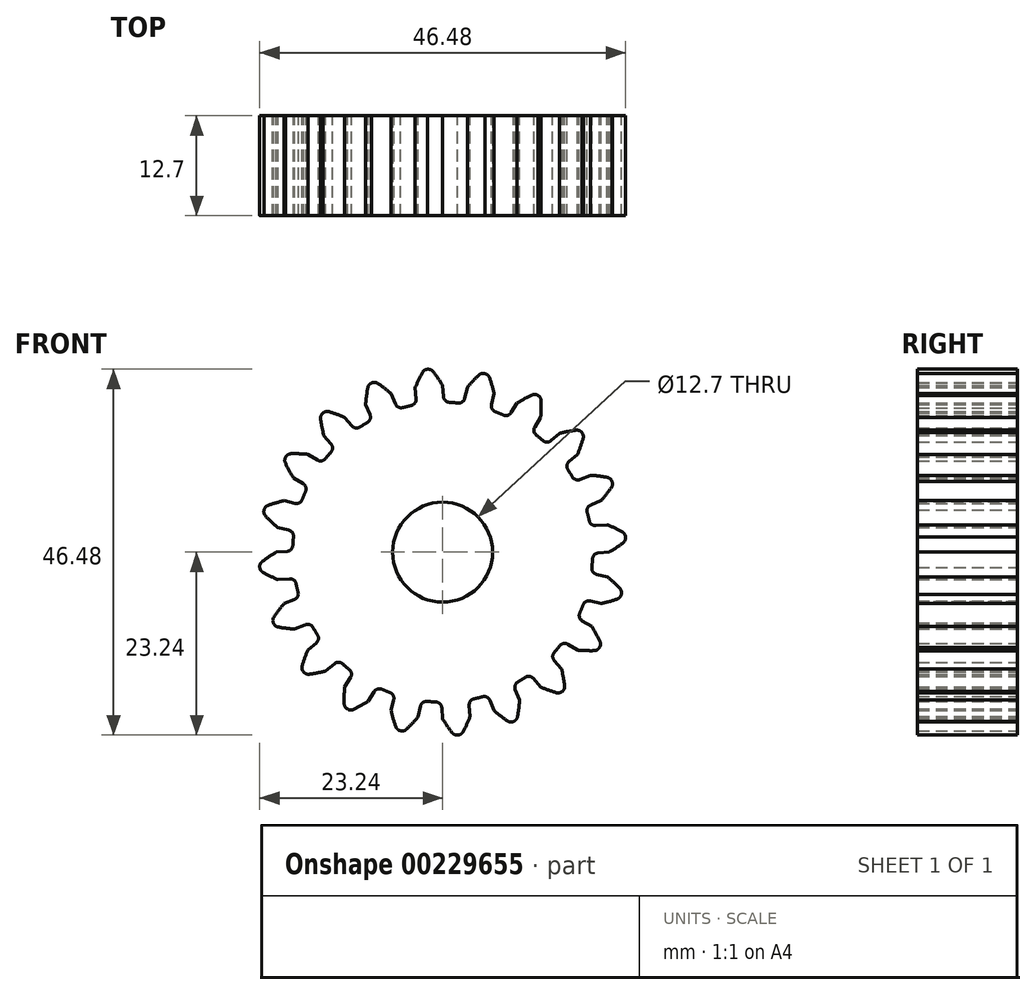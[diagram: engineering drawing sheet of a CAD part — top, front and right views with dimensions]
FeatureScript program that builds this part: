
annotation { "Feature Type Name" : "Feature", "Feature Type Description" : "" }
export const myFeature = defineFeature(function(context is Context, id is Id, definition is map)
    precondition{}
    {
        {
            var Q0;
            Q0=qCreatedBy(makeId("Front.planeOp"),FACE);
            var sketch = newSketch(context, id + "F0", { "sketchPlane" : qUnion([Q0])});
            skArc(sketch, "E0", {"start": v(-4, 18.63) * mm, "mid": v(-12.3, -14.54) * mm, "end": v(19.03, -0.86) * mm});
            skArc(sketch, "E1.trimOffspring", {"start": v(0, 21.17) * mm, "mid": v(-0.57, 22.06) * mm, "end": v(-1.2, 22.93) * mm});
            skLineSegment(sketch, "E2", {"start": v(-1.82, 23.24) * mm, "end": v(-1.92, 23.24) * mm});
            skLineSegment(sketch, "E3", {"start": v(0, 21.17) * mm, "end": v(0.11, 19.76) * mm});
            skLineSegment(sketch, "E4.MirrorCS", {"start": v(-2.01, 23.22) * mm, "end": v(-1.92, 23.24) * mm});
            skArc(sketch, "E5.MirrorCS", {"start": v(-3.49, 20.9) * mm, "mid": v(-3.06, 21.87) * mm, "end": v(-2.58, 22.82) * mm});
            skLineSegment(sketch, "E6.MirrorCS", {"start": v(-3.49, 20.9) * mm, "end": v(-3.38, 19.46) * mm});
            skPoint(sketch, "E7.visualSharp", {"position": v(0.17, 19.05) * mm});
            skArc(sketch, "E7.filletArc", {"start": v(0.11, 19.76) * mm, "mid": v(0.35, 19.25) * mm, "end": v(0.86, 19.03) * mm});
            skPoint(sketch, "E8.visualSharp", {"position": v(-3.32, 18.76) * mm});
            skArc(sketch, "E8.filletArc", {"start": v(-4, 18.63) * mm, "mid": v(-3.53, 18.93) * mm, "end": v(-3.38, 19.46) * mm});
            skPoint(sketch, "E9.visualSharp", {"position": v(-2.39, 23.16) * mm});
            skArc(sketch, "E9.filletArc", {"start": v(-2.01, 23.22) * mm, "mid": v(-2.34, 23.09) * mm, "end": v(-2.58, 22.82) * mm});
            skPoint(sketch, "E10.visualSharp", {"position": v(-1.44, 23.24) * mm});
            skArc(sketch, "E10.filletArc", {"start": v(-1.2, 22.93) * mm, "mid": v(-1.47, 23.16) * mm, "end": v(-1.82, 23.24) * mm});
            skArc(sketch, "E11.1.0", {"start": v(-9.56, 16.48) * mm, "mid": v(-9.2, 16.9) * mm, "end": v(-9.22, 17.46) * mm});
            skLineSegment(sketch, "E11.1.1", {"start": v(-9.77, 18.8) * mm, "end": v(-9.22, 17.46) * mm});
            skArc(sketch, "E11.1.2", {"start": v(-9.77, 18.8) * mm, "mid": v(-9.67, 19.85) * mm, "end": v(-9.5, 20.9) * mm});
            skArc(sketch, "E11.1.3", {"start": v(-9.09, 21.47) * mm, "mid": v(-9.36, 21.24) * mm, "end": v(-9.5, 20.9) * mm});
            skLineSegment(sketch, "E11.1.4", {"start": v(-9.09, 21.47) * mm, "end": v(-9, 21.5) * mm});
            skLineSegment(sketch, "E11.1.5", {"start": v(-8.92, 21.54) * mm, "end": v(-9, 21.5) * mm});
            skArc(sketch, "E11.1.6", {"start": v(-8.23, 21.44) * mm, "mid": v(-8.56, 21.57) * mm, "end": v(-8.92, 21.54) * mm});
            skArc(sketch, "E11.1.7", {"start": v(-6.54, 20.13) * mm, "mid": v(-7.36, 20.8) * mm, "end": v(-8.23, 21.44) * mm});
            skLineSegment(sketch, "E11.1.8", {"start": v(-6.54, 20.13) * mm, "end": v(-6, 18.82) * mm});
            skArc(sketch, "E11.1.9", {"start": v(-6, 18.82) * mm, "mid": v(-5.62, 18.42) * mm, "end": v(-5.06, 18.37) * mm});
            skArc(sketch, "E11.2.0", {"start": v(-14.18, 12.72) * mm, "mid": v(-13.98, 13.24) * mm, "end": v(-14.17, 13.76) * mm});
            skLineSegment(sketch, "E11.2.1", {"start": v(-15.1, 14.85) * mm, "end": v(-14.17, 13.76) * mm});
            skArc(sketch, "E11.2.2", {"start": v(-15.1, 14.85) * mm, "mid": v(-15.33, 15.9) * mm, "end": v(-15.5, 16.95) * mm});
            skArc(sketch, "E11.2.3", {"start": v(-15.28, 17.6) * mm, "mid": v(-15.47, 17.3) * mm, "end": v(-15.5, 16.95) * mm});
            skLineSegment(sketch, "E11.2.4", {"start": v(-15.28, 17.6) * mm, "end": v(-15.21, 17.67) * mm});
            skLineSegment(sketch, "E11.2.5", {"start": v(-15.13, 17.73) * mm, "end": v(-15.21, 17.67) * mm});
            skArc(sketch, "E11.2.6", {"start": v(-14.45, 17.85) * mm, "mid": v(-14.8, 17.87) * mm, "end": v(-15.13, 17.73) * mm});
            skArc(sketch, "E11.2.7", {"start": v(-12.44, 17.12) * mm, "mid": v(-13.43, 17.51) * mm, "end": v(-14.45, 17.85) * mm});
            skLineSegment(sketch, "E11.2.8", {"start": v(-12.44, 17.12) * mm, "end": v(-11.52, 16.05) * mm});
            skArc(sketch, "E11.2.9", {"start": v(-11.52, 16.05) * mm, "mid": v(-11.03, 15.78) * mm, "end": v(-10.49, 15.9) * mm});
            skArc(sketch, "E11.3.0", {"start": v(-17.42, 7.72) * mm, "mid": v(-17.39, 8.27) * mm, "end": v(-17.73, 8.7) * mm});
            skLineSegment(sketch, "E11.3.1", {"start": v(-18.95, 9.46) * mm, "end": v(-17.73, 8.7) * mm});
            skArc(sketch, "E11.3.2", {"start": v(-18.95, 9.46) * mm, "mid": v(-19.5, 10.38) * mm, "end": v(-19.98, 11.33) * mm});
            skArc(sketch, "E11.3.3", {"start": v(-19.97, 12.02) * mm, "mid": v(-20.06, 11.68) * mm, "end": v(-19.98, 11.33) * mm});
            skLineSegment(sketch, "E11.3.4", {"start": v(-19.97, 12.02) * mm, "end": v(-19.93, 12.1) * mm});
            skLineSegment(sketch, "E11.3.5", {"start": v(-19.87, 12.18) * mm, "end": v(-19.93, 12.1) * mm});
            skArc(sketch, "E11.3.6", {"start": v(-19.25, 12.5) * mm, "mid": v(-19.6, 12.42) * mm, "end": v(-19.87, 12.18) * mm});
            skArc(sketch, "E11.3.7", {"start": v(-17.12, 12.44) * mm, "mid": v(-18.19, 12.5) * mm, "end": v(-19.25, 12.5) * mm});
            skLineSegment(sketch, "E11.3.8", {"start": v(-17.12, 12.44) * mm, "end": v(-15.92, 11.7) * mm});
            skArc(sketch, "E11.3.9", {"start": v(-15.92, 11.7) * mm, "mid": v(-15.37, 11.6) * mm, "end": v(-14.9, 11.88) * mm});
            skArc(sketch, "E11.4.0", {"start": v(-18.95, 1.96) * mm, "mid": v(-19.09, 2.5) * mm, "end": v(-19.55, 2.8) * mm});
            skLineSegment(sketch, "E11.4.1", {"start": v(-20.95, 3.14) * mm, "end": v(-19.55, 2.8) * mm});
            skArc(sketch, "E11.4.2", {"start": v(-20.95, 3.14) * mm, "mid": v(-21.74, 3.85) * mm, "end": v(-22.5, 4.6) * mm});
            skArc(sketch, "E11.4.3", {"start": v(-22.7, 5.26) * mm, "mid": v(-22.68, 4.9) * mm, "end": v(-22.5, 4.6) * mm});
            skLineSegment(sketch, "E11.4.4", {"start": v(-22.7, 5.26) * mm, "end": v(-22.7, 5.36) * mm});
            skLineSegment(sketch, "E11.4.5", {"start": v(-22.66, 5.45) * mm, "end": v(-22.7, 5.36) * mm});
            skArc(sketch, "E11.4.6", {"start": v(-22.18, 5.95) * mm, "mid": v(-22.48, 5.75) * mm, "end": v(-22.66, 5.45) * mm});
            skArc(sketch, "E11.4.7", {"start": v(-20.13, 6.54) * mm, "mid": v(-21.16, 6.27) * mm, "end": v(-22.18, 5.95) * mm});
            skLineSegment(sketch, "E11.4.8", {"start": v(-20.13, 6.54) * mm, "end": v(-18.75, 6.21) * mm});
            skArc(sketch, "E11.4.9", {"start": v(-18.75, 6.21) * mm, "mid": v(-18.2, 6.28) * mm, "end": v(-17.83, 6.7) * mm});
            skArc(sketch, "E11.5.0", {"start": v(-18.63, -4) * mm, "mid": v(-18.93, -3.53) * mm, "end": v(-19.46, -3.38) * mm});
            skLineSegment(sketch, "E11.5.1", {"start": v(-20.9, -3.49) * mm, "end": v(-19.46, -3.38) * mm});
            skArc(sketch, "E11.5.2", {"start": v(-20.9, -3.49) * mm, "mid": v(-21.87, -3.06) * mm, "end": v(-22.82, -2.58) * mm});
            skArc(sketch, "E11.5.3", {"start": v(-23.22, -2.01) * mm, "mid": v(-23.09, -2.34) * mm, "end": v(-22.82, -2.58) * mm});
            skLineSegment(sketch, "E11.5.4", {"start": v(-23.22, -2.01) * mm, "end": v(-23.24, -1.92) * mm});
            skLineSegment(sketch, "E11.5.5", {"start": v(-23.24, -1.82) * mm, "end": v(-23.24, -1.92) * mm});
            skArc(sketch, "E11.5.6", {"start": v(-22.93, -1.2) * mm, "mid": v(-23.16, -1.47) * mm, "end": v(-23.24, -1.82) * mm});
            skArc(sketch, "E11.5.7", {"start": v(-21.17, 0) * mm, "mid": v(-22.06, -0.57) * mm, "end": v(-22.93, -1.2) * mm});
            skLineSegment(sketch, "E11.5.8", {"start": v(-21.17, 0) * mm, "end": v(-19.76, 0.11) * mm});
            skArc(sketch, "E11.5.9", {"start": v(-19.76, 0.11) * mm, "mid": v(-19.25, 0.35) * mm, "end": v(-19.03, 0.86) * mm});
            skArc(sketch, "E11.6.0", {"start": v(-16.48, -9.56) * mm, "mid": v(-16.9, -9.2) * mm, "end": v(-17.46, -9.22) * mm});
            skLineSegment(sketch, "E11.6.1", {"start": v(-18.8, -9.77) * mm, "end": v(-17.46, -9.22) * mm});
            skArc(sketch, "E11.6.2", {"start": v(-18.8, -9.77) * mm, "mid": v(-19.85, -9.67) * mm, "end": v(-20.9, -9.5) * mm});
            skArc(sketch, "E11.6.3", {"start": v(-21.47, -9.09) * mm, "mid": v(-21.24, -9.36) * mm, "end": v(-20.9, -9.5) * mm});
            skLineSegment(sketch, "E11.6.4", {"start": v(-21.47, -9.09) * mm, "end": v(-21.5, -9) * mm});
            skLineSegment(sketch, "E11.6.5", {"start": v(-21.54, -8.92) * mm, "end": v(-21.5, -9) * mm});
            skArc(sketch, "E11.6.6", {"start": v(-21.44, -8.23) * mm, "mid": v(-21.57, -8.56) * mm, "end": v(-21.54, -8.92) * mm});
            skArc(sketch, "E11.6.7", {"start": v(-20.13, -6.54) * mm, "mid": v(-20.8, -7.36) * mm, "end": v(-21.44, -8.23) * mm});
            skLineSegment(sketch, "E11.6.8", {"start": v(-20.13, -6.54) * mm, "end": v(-18.82, -6) * mm});
            skArc(sketch, "E11.6.9", {"start": v(-18.82, -6) * mm, "mid": v(-18.42, -5.62) * mm, "end": v(-18.37, -5.06) * mm});
            skArc(sketch, "E11.7.0", {"start": v(-12.72, -14.18) * mm, "mid": v(-13.24, -13.98) * mm, "end": v(-13.76, -14.17) * mm});
            skLineSegment(sketch, "E11.7.1", {"start": v(-14.85, -15.1) * mm, "end": v(-13.76, -14.17) * mm});
            skArc(sketch, "E11.7.2", {"start": v(-14.85, -15.1) * mm, "mid": v(-15.9, -15.33) * mm, "end": v(-16.95, -15.5) * mm});
            skArc(sketch, "E11.7.3", {"start": v(-17.6, -15.28) * mm, "mid": v(-17.3, -15.47) * mm, "end": v(-16.95, -15.5) * mm});
            skLineSegment(sketch, "E11.7.4", {"start": v(-17.6, -15.28) * mm, "end": v(-17.67, -15.21) * mm});
            skLineSegment(sketch, "E11.7.5", {"start": v(-17.73, -15.13) * mm, "end": v(-17.67, -15.21) * mm});
            skArc(sketch, "E11.7.6", {"start": v(-17.85, -14.45) * mm, "mid": v(-17.87, -14.8) * mm, "end": v(-17.73, -15.13) * mm});
            skArc(sketch, "E11.7.7", {"start": v(-17.12, -12.44) * mm, "mid": v(-17.51, -13.43) * mm, "end": v(-17.85, -14.45) * mm});
            skLineSegment(sketch, "E11.7.8", {"start": v(-17.12, -12.44) * mm, "end": v(-16.05, -11.52) * mm});
            skArc(sketch, "E11.7.9", {"start": v(-16.05, -11.52) * mm, "mid": v(-15.78, -11.03) * mm, "end": v(-15.9, -10.49) * mm});
            skArc(sketch, "E11.8.0", {"start": v(-7.72, -17.42) * mm, "mid": v(-8.27, -17.39) * mm, "end": v(-8.7, -17.73) * mm});
            skLineSegment(sketch, "E11.8.1", {"start": v(-9.46, -18.95) * mm, "end": v(-8.7, -17.73) * mm});
            skArc(sketch, "E11.8.2", {"start": v(-9.46, -18.95) * mm, "mid": v(-10.38, -19.5) * mm, "end": v(-11.33, -19.98) * mm});
            skArc(sketch, "E11.8.3", {"start": v(-12.02, -19.97) * mm, "mid": v(-11.68, -20.06) * mm, "end": v(-11.33, -19.98) * mm});
            skLineSegment(sketch, "E11.8.4", {"start": v(-12.02, -19.97) * mm, "end": v(-12.1, -19.93) * mm});
            skLineSegment(sketch, "E11.8.5", {"start": v(-12.18, -19.87) * mm, "end": v(-12.1, -19.93) * mm});
            skArc(sketch, "E11.8.6", {"start": v(-12.5, -19.25) * mm, "mid": v(-12.42, -19.6) * mm, "end": v(-12.18, -19.87) * mm});
            skArc(sketch, "E11.8.7", {"start": v(-12.44, -17.12) * mm, "mid": v(-12.5, -18.19) * mm, "end": v(-12.5, -19.25) * mm});
            skLineSegment(sketch, "E11.8.8", {"start": v(-12.44, -17.12) * mm, "end": v(-11.7, -15.92) * mm});
            skArc(sketch, "E11.8.9", {"start": v(-11.7, -15.92) * mm, "mid": v(-11.6, -15.37) * mm, "end": v(-11.88, -14.9) * mm});
            skArc(sketch, "E11.9.0", {"start": v(-1.96, -18.95) * mm, "mid": v(-2.5, -19.09) * mm, "end": v(-2.8, -19.55) * mm});
            skLineSegment(sketch, "E11.9.1", {"start": v(-3.14, -20.95) * mm, "end": v(-2.8, -19.55) * mm});
            skArc(sketch, "E11.9.2", {"start": v(-3.14, -20.95) * mm, "mid": v(-3.85, -21.74) * mm, "end": v(-4.6, -22.5) * mm});
            skArc(sketch, "E11.9.3", {"start": v(-5.26, -22.7) * mm, "mid": v(-4.9, -22.68) * mm, "end": v(-4.6, -22.5) * mm});
            skLineSegment(sketch, "E11.9.4", {"start": v(-5.26, -22.7) * mm, "end": v(-5.36, -22.7) * mm});
            skLineSegment(sketch, "E11.9.5", {"start": v(-5.45, -22.66) * mm, "end": v(-5.36, -22.7) * mm});
            skArc(sketch, "E11.9.6", {"start": v(-5.95, -22.18) * mm, "mid": v(-5.75, -22.48) * mm, "end": v(-5.45, -22.66) * mm});
            skArc(sketch, "E11.9.7", {"start": v(-6.54, -20.13) * mm, "mid": v(-6.27, -21.16) * mm, "end": v(-5.95, -22.18) * mm});
            skLineSegment(sketch, "E11.9.8", {"start": v(-6.54, -20.13) * mm, "end": v(-6.21, -18.75) * mm});
            skArc(sketch, "E11.9.9", {"start": v(-6.21, -18.75) * mm, "mid": v(-6.28, -18.2) * mm, "end": v(-6.7, -17.83) * mm});
            skArc(sketch, "E11.10.0", {"start": v(4, -18.63) * mm, "mid": v(3.53, -18.93) * mm, "end": v(3.38, -19.46) * mm});
            skLineSegment(sketch, "E11.10.1", {"start": v(3.49, -20.9) * mm, "end": v(3.38, -19.46) * mm});
            skArc(sketch, "E11.10.2", {"start": v(3.49, -20.9) * mm, "mid": v(3.06, -21.87) * mm, "end": v(2.58, -22.82) * mm});
            skArc(sketch, "E11.10.3", {"start": v(2.01, -23.22) * mm, "mid": v(2.34, -23.09) * mm, "end": v(2.58, -22.82) * mm});
            skLineSegment(sketch, "E11.10.4", {"start": v(2.01, -23.22) * mm, "end": v(1.92, -23.24) * mm});
            skLineSegment(sketch, "E11.10.5", {"start": v(1.82, -23.24) * mm, "end": v(1.92, -23.24) * mm});
            skArc(sketch, "E11.10.6", {"start": v(1.2, -22.93) * mm, "mid": v(1.47, -23.16) * mm, "end": v(1.82, -23.24) * mm});
            skArc(sketch, "E11.10.7", {"start": v(0, -21.17) * mm, "mid": v(0.57, -22.06) * mm, "end": v(1.2, -22.93) * mm});
            skLineSegment(sketch, "E11.10.8", {"start": v(0, -21.17) * mm, "end": v(-0.11, -19.76) * mm});
            skArc(sketch, "E11.10.9", {"start": v(-0.11, -19.76) * mm, "mid": v(-0.35, -19.25) * mm, "end": v(-0.86, -19.03) * mm});
            skArc(sketch, "E11.11.0", {"start": v(9.56, -16.48) * mm, "mid": v(9.2, -16.9) * mm, "end": v(9.22, -17.46) * mm});
            skLineSegment(sketch, "E11.11.1", {"start": v(9.77, -18.8) * mm, "end": v(9.22, -17.46) * mm});
            skArc(sketch, "E11.11.2", {"start": v(9.77, -18.8) * mm, "mid": v(9.67, -19.85) * mm, "end": v(9.5, -20.9) * mm});
            skArc(sketch, "E11.11.3", {"start": v(9.09, -21.47) * mm, "mid": v(9.36, -21.24) * mm, "end": v(9.5, -20.9) * mm});
            skLineSegment(sketch, "E11.11.4", {"start": v(9.09, -21.47) * mm, "end": v(9, -21.5) * mm});
            skLineSegment(sketch, "E11.11.5", {"start": v(8.92, -21.54) * mm, "end": v(9, -21.5) * mm});
            skArc(sketch, "E11.11.6", {"start": v(8.23, -21.44) * mm, "mid": v(8.56, -21.57) * mm, "end": v(8.92, -21.54) * mm});
            skArc(sketch, "E11.11.7", {"start": v(6.54, -20.13) * mm, "mid": v(7.36, -20.8) * mm, "end": v(8.23, -21.44) * mm});
            skLineSegment(sketch, "E11.11.8", {"start": v(6.54, -20.13) * mm, "end": v(6, -18.82) * mm});
            skArc(sketch, "E11.11.9", {"start": v(6, -18.82) * mm, "mid": v(5.62, -18.42) * mm, "end": v(5.06, -18.37) * mm});
            skArc(sketch, "E11.12.0", {"start": v(14.18, -12.72) * mm, "mid": v(13.98, -13.24) * mm, "end": v(14.17, -13.76) * mm});
            skLineSegment(sketch, "E11.12.1", {"start": v(15.1, -14.85) * mm, "end": v(14.17, -13.76) * mm});
            skArc(sketch, "E11.12.2", {"start": v(15.1, -14.85) * mm, "mid": v(15.33, -15.9) * mm, "end": v(15.5, -16.95) * mm});
            skArc(sketch, "E11.12.3", {"start": v(15.28, -17.6) * mm, "mid": v(15.47, -17.3) * mm, "end": v(15.5, -16.95) * mm});
            skLineSegment(sketch, "E11.12.4", {"start": v(15.28, -17.6) * mm, "end": v(15.21, -17.67) * mm});
            skLineSegment(sketch, "E11.12.5", {"start": v(15.13, -17.73) * mm, "end": v(15.21, -17.67) * mm});
            skArc(sketch, "E11.12.6", {"start": v(14.45, -17.85) * mm, "mid": v(14.8, -17.87) * mm, "end": v(15.13, -17.73) * mm});
            skArc(sketch, "E11.12.7", {"start": v(12.44, -17.12) * mm, "mid": v(13.43, -17.51) * mm, "end": v(14.45, -17.85) * mm});
            skLineSegment(sketch, "E11.12.8", {"start": v(12.44, -17.12) * mm, "end": v(11.52, -16.05) * mm});
            skArc(sketch, "E11.12.9", {"start": v(11.52, -16.05) * mm, "mid": v(11.03, -15.78) * mm, "end": v(10.49, -15.9) * mm});
            skArc(sketch, "E11.13.0", {"start": v(17.42, -7.72) * mm, "mid": v(17.39, -8.27) * mm, "end": v(17.73, -8.7) * mm});
            skLineSegment(sketch, "E11.13.1", {"start": v(18.95, -9.46) * mm, "end": v(17.73, -8.7) * mm});
            skArc(sketch, "E11.13.2", {"start": v(18.95, -9.46) * mm, "mid": v(19.5, -10.38) * mm, "end": v(19.98, -11.33) * mm});
            skArc(sketch, "E11.13.3", {"start": v(19.97, -12.02) * mm, "mid": v(20.06, -11.68) * mm, "end": v(19.98, -11.33) * mm});
            skLineSegment(sketch, "E11.13.4", {"start": v(19.97, -12.02) * mm, "end": v(19.93, -12.1) * mm});
            skLineSegment(sketch, "E11.13.5", {"start": v(19.87, -12.18) * mm, "end": v(19.93, -12.1) * mm});
            skArc(sketch, "E11.13.6", {"start": v(19.25, -12.5) * mm, "mid": v(19.6, -12.42) * mm, "end": v(19.87, -12.18) * mm});
            skArc(sketch, "E11.13.7", {"start": v(17.12, -12.44) * mm, "mid": v(18.19, -12.5) * mm, "end": v(19.25, -12.5) * mm});
            skLineSegment(sketch, "E11.13.8", {"start": v(17.12, -12.44) * mm, "end": v(15.92, -11.7) * mm});
            skArc(sketch, "E11.13.9", {"start": v(15.92, -11.7) * mm, "mid": v(15.37, -11.6) * mm, "end": v(14.9, -11.88) * mm});
            skArc(sketch, "E11.14.0", {"start": v(18.95, -1.96) * mm, "mid": v(19.09, -2.5) * mm, "end": v(19.55, -2.8) * mm});
            skLineSegment(sketch, "E11.14.1", {"start": v(20.95, -3.14) * mm, "end": v(19.55, -2.8) * mm});
            skArc(sketch, "E11.14.2", {"start": v(20.95, -3.14) * mm, "mid": v(21.74, -3.85) * mm, "end": v(22.5, -4.6) * mm});
            skArc(sketch, "E11.14.3", {"start": v(22.7, -5.26) * mm, "mid": v(22.68, -4.9) * mm, "end": v(22.5, -4.6) * mm});
            skLineSegment(sketch, "E11.14.4", {"start": v(22.7, -5.26) * mm, "end": v(22.7, -5.36) * mm});
            skLineSegment(sketch, "E11.14.5", {"start": v(22.66, -5.45) * mm, "end": v(22.7, -5.36) * mm});
            skArc(sketch, "E11.14.6", {"start": v(22.18, -5.95) * mm, "mid": v(22.48, -5.75) * mm, "end": v(22.66, -5.45) * mm});
            skArc(sketch, "E11.14.7", {"start": v(20.13, -6.54) * mm, "mid": v(21.16, -6.27) * mm, "end": v(22.18, -5.95) * mm});
            skLineSegment(sketch, "E11.14.8", {"start": v(20.13, -6.54) * mm, "end": v(18.75, -6.21) * mm});
            skArc(sketch, "E11.14.9", {"start": v(18.75, -6.21) * mm, "mid": v(18.2, -6.28) * mm, "end": v(17.83, -6.7) * mm});
            skArc(sketch, "E11.15.0", {"start": v(18.63, 4) * mm, "mid": v(18.93, 3.53) * mm, "end": v(19.46, 3.38) * mm});
            skLineSegment(sketch, "E11.15.1", {"start": v(20.9, 3.49) * mm, "end": v(19.46, 3.38) * mm});
            skArc(sketch, "E11.15.2", {"start": v(20.9, 3.49) * mm, "mid": v(21.87, 3.06) * mm, "end": v(22.82, 2.58) * mm});
            skArc(sketch, "E11.15.3", {"start": v(23.22, 2.01) * mm, "mid": v(23.09, 2.34) * mm, "end": v(22.82, 2.58) * mm});
            skLineSegment(sketch, "E11.15.4", {"start": v(23.22, 2.01) * mm, "end": v(23.24, 1.92) * mm});
            skLineSegment(sketch, "E11.15.5", {"start": v(23.24, 1.82) * mm, "end": v(23.24, 1.92) * mm});
            skArc(sketch, "E11.15.6", {"start": v(22.93, 1.2) * mm, "mid": v(23.16, 1.47) * mm, "end": v(23.24, 1.82) * mm});
            skArc(sketch, "E11.15.7", {"start": v(21.17, 0) * mm, "mid": v(22.06, 0.57) * mm, "end": v(22.93, 1.2) * mm});
            skLineSegment(sketch, "E11.15.8", {"start": v(21.17, 0) * mm, "end": v(19.76, -0.11) * mm});
            skArc(sketch, "E11.15.9", {"start": v(19.76, -0.11) * mm, "mid": v(19.25, -0.35) * mm, "end": v(19.03, -0.86) * mm});
            skArc(sketch, "E11.16.0", {"start": v(16.48, 9.56) * mm, "mid": v(16.9, 9.2) * mm, "end": v(17.46, 9.22) * mm});
            skLineSegment(sketch, "E11.16.1", {"start": v(18.8, 9.77) * mm, "end": v(17.46, 9.22) * mm});
            skArc(sketch, "E11.16.2", {"start": v(18.8, 9.77) * mm, "mid": v(19.85, 9.67) * mm, "end": v(20.9, 9.5) * mm});
            skArc(sketch, "E11.16.3", {"start": v(21.47, 9.09) * mm, "mid": v(21.24, 9.36) * mm, "end": v(20.9, 9.5) * mm});
            skLineSegment(sketch, "E11.16.4", {"start": v(21.47, 9.09) * mm, "end": v(21.5, 9) * mm});
            skLineSegment(sketch, "E11.16.5", {"start": v(21.54, 8.92) * mm, "end": v(21.5, 9) * mm});
            skArc(sketch, "E11.16.6", {"start": v(21.44, 8.23) * mm, "mid": v(21.57, 8.56) * mm, "end": v(21.54, 8.92) * mm});
            skArc(sketch, "E11.16.7", {"start": v(20.13, 6.54) * mm, "mid": v(20.8, 7.36) * mm, "end": v(21.44, 8.23) * mm});
            skLineSegment(sketch, "E11.16.8", {"start": v(20.13, 6.54) * mm, "end": v(18.82, 6) * mm});
            skArc(sketch, "E11.16.9", {"start": v(18.82, 6) * mm, "mid": v(18.42, 5.62) * mm, "end": v(18.37, 5.06) * mm});
            skArc(sketch, "E11.17.0", {"start": v(12.72, 14.18) * mm, "mid": v(13.24, 13.98) * mm, "end": v(13.76, 14.17) * mm});
            skLineSegment(sketch, "E11.17.1", {"start": v(14.85, 15.1) * mm, "end": v(13.76, 14.17) * mm});
            skArc(sketch, "E11.17.2", {"start": v(14.85, 15.1) * mm, "mid": v(15.9, 15.33) * mm, "end": v(16.95, 15.5) * mm});
            skArc(sketch, "E11.17.3", {"start": v(17.6, 15.28) * mm, "mid": v(17.3, 15.47) * mm, "end": v(16.95, 15.5) * mm});
            skLineSegment(sketch, "E11.17.4", {"start": v(17.6, 15.28) * mm, "end": v(17.67, 15.21) * mm});
            skLineSegment(sketch, "E11.17.5", {"start": v(17.73, 15.13) * mm, "end": v(17.67, 15.21) * mm});
            skArc(sketch, "E11.17.6", {"start": v(17.85, 14.45) * mm, "mid": v(17.87, 14.8) * mm, "end": v(17.73, 15.13) * mm});
            skArc(sketch, "E11.17.7", {"start": v(17.12, 12.44) * mm, "mid": v(17.51, 13.43) * mm, "end": v(17.85, 14.45) * mm});
            skLineSegment(sketch, "E11.17.8", {"start": v(17.12, 12.44) * mm, "end": v(16.05, 11.52) * mm});
            skArc(sketch, "E11.17.9", {"start": v(16.05, 11.52) * mm, "mid": v(15.78, 11.03) * mm, "end": v(15.9, 10.49) * mm});
            skArc(sketch, "E11.18.0", {"start": v(7.72, 17.42) * mm, "mid": v(8.27, 17.39) * mm, "end": v(8.7, 17.73) * mm});
            skLineSegment(sketch, "E11.18.1", {"start": v(9.46, 18.95) * mm, "end": v(8.7, 17.73) * mm});
            skArc(sketch, "E11.18.2", {"start": v(9.46, 18.95) * mm, "mid": v(10.38, 19.5) * mm, "end": v(11.33, 19.98) * mm});
            skArc(sketch, "E11.18.3", {"start": v(12.02, 19.97) * mm, "mid": v(11.68, 20.06) * mm, "end": v(11.33, 19.98) * mm});
            skLineSegment(sketch, "E11.18.4", {"start": v(12.02, 19.97) * mm, "end": v(12.1, 19.93) * mm});
            skLineSegment(sketch, "E11.18.5", {"start": v(12.18, 19.87) * mm, "end": v(12.1, 19.93) * mm});
            skArc(sketch, "E11.18.6", {"start": v(12.5, 19.25) * mm, "mid": v(12.42, 19.6) * mm, "end": v(12.18, 19.87) * mm});
            skArc(sketch, "E11.18.7", {"start": v(12.44, 17.12) * mm, "mid": v(12.5, 18.19) * mm, "end": v(12.5, 19.25) * mm});
            skLineSegment(sketch, "E11.18.8", {"start": v(12.44, 17.12) * mm, "end": v(11.7, 15.92) * mm});
            skArc(sketch, "E11.18.9", {"start": v(11.7, 15.92) * mm, "mid": v(11.6, 15.37) * mm, "end": v(11.88, 14.9) * mm});
            skArc(sketch, "E11.19.0", {"start": v(1.96, 18.95) * mm, "mid": v(2.5, 19.09) * mm, "end": v(2.8, 19.55) * mm});
            skLineSegment(sketch, "E11.19.1", {"start": v(3.14, 20.95) * mm, "end": v(2.8, 19.55) * mm});
            skArc(sketch, "E11.19.2", {"start": v(3.14, 20.95) * mm, "mid": v(3.85, 21.74) * mm, "end": v(4.6, 22.5) * mm});
            skArc(sketch, "E11.19.3", {"start": v(5.26, 22.7) * mm, "mid": v(4.9, 22.68) * mm, "end": v(4.6, 22.5) * mm});
            skLineSegment(sketch, "E11.19.4", {"start": v(5.26, 22.7) * mm, "end": v(5.36, 22.7) * mm});
            skLineSegment(sketch, "E11.19.5", {"start": v(5.45, 22.66) * mm, "end": v(5.36, 22.7) * mm});
            skArc(sketch, "E11.19.6", {"start": v(5.95, 22.18) * mm, "mid": v(5.75, 22.48) * mm, "end": v(5.45, 22.66) * mm});
            skArc(sketch, "E11.19.7", {"start": v(6.54, 20.13) * mm, "mid": v(6.27, 21.16) * mm, "end": v(5.95, 22.18) * mm});
            skLineSegment(sketch, "E11.19.8", {"start": v(6.54, 20.13) * mm, "end": v(6.21, 18.75) * mm});
            skArc(sketch, "E11.19.9", {"start": v(6.21, 18.75) * mm, "mid": v(6.28, 18.2) * mm, "end": v(6.7, 17.83) * mm});
            skArc(sketch, "E12.trimOffspring", {"start": v(1.96, 18.95) * mm, "mid": v(1.4, 19) * mm, "end": v(0.86, 19.03) * mm});
            skArc(sketch, "E13.trimOffspring", {"start": v(7.72, 17.42) * mm, "mid": v(7.21, 17.63) * mm, "end": v(6.7, 17.83) * mm});
            skArc(sketch, "E14.trimOffspring", {"start": v(12.72, 14.18) * mm, "mid": v(12.3, 14.54) * mm, "end": v(11.88, 14.9) * mm});
            skArc(sketch, "E15.trimOffspring", {"start": v(16.48, 9.56) * mm, "mid": v(16.2, 10.03) * mm, "end": v(15.9, 10.49) * mm});
            skArc(sketch, "E16.trimOffspring", {"start": v(18.63, 4) * mm, "mid": v(18.5, 4.53) * mm, "end": v(18.37, 5.06) * mm});
            skSolve(sketch);
        }
        {
            var Q0;
            Q0 = qSketchRegion(id + "F0", true);
            extrude(context, id + "F1", {"entities" : qUnion([Q0]), "depth" : 12.7 * mm});
        }
        {
            var Q0;
            Q0=makeQuery(id+"F1.opExtrude","CAP_FACE",FACE,{"disambiguationData":[OSD([sQuery(id+"F0.wireOp",EDGE,"E0"),sQuery(id+"F0.wireOp",EDGE,"E1.trimOffspring"),sQuery(id+"F0.wireOp",EDGE,"E2"),sQuery(id+"F0.wireOp",EDGE,"E3"),sQuery(id+"F0.wireOp",EDGE,"E4.MirrorCS"),sQuery(id+"F0.wireOp",EDGE,"E5.MirrorCS"),sQuery(id+"F0.wireOp",EDGE,"E6.MirrorCS"),sQuery(id+"F0.wireOp",EDGE,"E7.filletArc"),sQuery(id+"F0.wireOp",EDGE,"E8.filletArc"),sQuery(id+"F0.wireOp",EDGE,"E9.filletArc"),sQuery(id+"F0.wireOp",EDGE,"E10.filletArc"),sQuery(id+"F0.wireOp",EDGE,"E11.1.0"),sQuery(id+"F0.wireOp",EDGE,"E11.1.1"),sQuery(id+"F0.wireOp",EDGE,"E11.1.2"),sQuery(id+"F0.wireOp",EDGE,"E11.1.3"),sQuery(id+"F0.wireOp",EDGE,"E11.1.4"),sQuery(id+"F0.wireOp",EDGE,"E11.1.5"),sQuery(id+"F0.wireOp",EDGE,"E11.1.6"),sQuery(id+"F0.wireOp",EDGE,"E11.1.7"),sQuery(id+"F0.wireOp",EDGE,"E11.1.8"),sQuery(id+"F0.wireOp",EDGE,"E11.1.9"),sQuery(id+"F0.wireOp",EDGE,"E11.2.0"),sQuery(id+"F0.wireOp",EDGE,"E11.2.1"),sQuery(id+"F0.wireOp",EDGE,"E11.2.2"),sQuery(id+"F0.wireOp",EDGE,"E11.2.3"),sQuery(id+"F0.wireOp",EDGE,"E11.2.4"),sQuery(id+"F0.wireOp",EDGE,"E11.2.5"),sQuery(id+"F0.wireOp",EDGE,"E11.2.6"),sQuery(id+"F0.wireOp",EDGE,"E11.2.7"),sQuery(id+"F0.wireOp",EDGE,"E11.2.8"),sQuery(id+"F0.wireOp",EDGE,"E11.2.9"),sQuery(id+"F0.wireOp",EDGE,"E11.3.0"),sQuery(id+"F0.wireOp",EDGE,"E11.3.1"),sQuery(id+"F0.wireOp",EDGE,"E11.3.2"),sQuery(id+"F0.wireOp",EDGE,"E11.3.3"),sQuery(id+"F0.wireOp",EDGE,"E11.3.4"),sQuery(id+"F0.wireOp",EDGE,"E11.3.5"),sQuery(id+"F0.wireOp",EDGE,"E11.3.6"),sQuery(id+"F0.wireOp",EDGE,"E11.3.7"),sQuery(id+"F0.wireOp",EDGE,"E11.3.8"),sQuery(id+"F0.wireOp",EDGE,"E11.3.9"),sQuery(id+"F0.wireOp",EDGE,"E11.4.0"),sQuery(id+"F0.wireOp",EDGE,"E11.4.1"),sQuery(id+"F0.wireOp",EDGE,"E11.4.2"),sQuery(id+"F0.wireOp",EDGE,"E11.4.3"),sQuery(id+"F0.wireOp",EDGE,"E11.4.4"),sQuery(id+"F0.wireOp",EDGE,"E11.4.5"),sQuery(id+"F0.wireOp",EDGE,"E11.4.6"),sQuery(id+"F0.wireOp",EDGE,"E11.4.7"),sQuery(id+"F0.wireOp",EDGE,"E11.4.8"),sQuery(id+"F0.wireOp",EDGE,"E11.4.9"),sQuery(id+"F0.wireOp",EDGE,"E11.5.0"),sQuery(id+"F0.wireOp",EDGE,"E11.5.1"),sQuery(id+"F0.wireOp",EDGE,"E11.5.2"),sQuery(id+"F0.wireOp",EDGE,"E11.5.3"),sQuery(id+"F0.wireOp",EDGE,"E11.5.4"),sQuery(id+"F0.wireOp",EDGE,"E11.5.5"),sQuery(id+"F0.wireOp",EDGE,"E11.5.6"),sQuery(id+"F0.wireOp",EDGE,"E11.5.7"),sQuery(id+"F0.wireOp",EDGE,"E11.5.8"),sQuery(id+"F0.wireOp",EDGE,"E11.5.9"),sQuery(id+"F0.wireOp",EDGE,"E11.6.0"),sQuery(id+"F0.wireOp",EDGE,"E11.6.1"),sQuery(id+"F0.wireOp",EDGE,"E11.6.2"),sQuery(id+"F0.wireOp",EDGE,"E11.6.3"),sQuery(id+"F0.wireOp",EDGE,"E11.6.4"),sQuery(id+"F0.wireOp",EDGE,"E11.6.5"),sQuery(id+"F0.wireOp",EDGE,"E11.6.6"),sQuery(id+"F0.wireOp",EDGE,"E11.6.7"),sQuery(id+"F0.wireOp",EDGE,"E11.6.8"),sQuery(id+"F0.wireOp",EDGE,"E11.6.9"),sQuery(id+"F0.wireOp",EDGE,"E11.7.0"),sQuery(id+"F0.wireOp",EDGE,"E11.7.1"),sQuery(id+"F0.wireOp",EDGE,"E11.7.2"),sQuery(id+"F0.wireOp",EDGE,"E11.7.3"),sQuery(id+"F0.wireOp",EDGE,"E11.7.4"),sQuery(id+"F0.wireOp",EDGE,"E11.7.5"),sQuery(id+"F0.wireOp",EDGE,"E11.7.6"),sQuery(id+"F0.wireOp",EDGE,"E11.7.7"),sQuery(id+"F0.wireOp",EDGE,"E11.7.8"),sQuery(id+"F0.wireOp",EDGE,"E11.7.9"),sQuery(id+"F0.wireOp",EDGE,"E11.8.0"),sQuery(id+"F0.wireOp",EDGE,"E11.8.1"),sQuery(id+"F0.wireOp",EDGE,"E11.8.2"),sQuery(id+"F0.wireOp",EDGE,"E11.8.3"),sQuery(id+"F0.wireOp",EDGE,"E11.8.4"),sQuery(id+"F0.wireOp",EDGE,"E11.8.5"),sQuery(id+"F0.wireOp",EDGE,"E11.8.6"),sQuery(id+"F0.wireOp",EDGE,"E11.8.7"),sQuery(id+"F0.wireOp",EDGE,"E11.8.8"),sQuery(id+"F0.wireOp",EDGE,"E11.8.9"),sQuery(id+"F0.wireOp",EDGE,"E11.9.0"),sQuery(id+"F0.wireOp",EDGE,"E11.9.1"),sQuery(id+"F0.wireOp",EDGE,"E11.9.2"),sQuery(id+"F0.wireOp",EDGE,"E11.9.3"),sQuery(id+"F0.wireOp",EDGE,"E11.9.4"),sQuery(id+"F0.wireOp",EDGE,"E11.9.5"),sQuery(id+"F0.wireOp",EDGE,"E11.9.6"),sQuery(id+"F0.wireOp",EDGE,"E11.9.7"),sQuery(id+"F0.wireOp",EDGE,"E11.9.8"),sQuery(id+"F0.wireOp",EDGE,"E11.9.9"),sQuery(id+"F0.wireOp",EDGE,"E11.10.0"),sQuery(id+"F0.wireOp",EDGE,"E11.10.1"),sQuery(id+"F0.wireOp",EDGE,"E11.10.2"),sQuery(id+"F0.wireOp",EDGE,"E11.10.3"),sQuery(id+"F0.wireOp",EDGE,"E11.10.4"),sQuery(id+"F0.wireOp",EDGE,"E11.10.5"),sQuery(id+"F0.wireOp",EDGE,"E11.10.6"),sQuery(id+"F0.wireOp",EDGE,"E11.10.7"),sQuery(id+"F0.wireOp",EDGE,"E11.10.8"),sQuery(id+"F0.wireOp",EDGE,"E11.10.9"),sQuery(id+"F0.wireOp",EDGE,"E11.11.0"),sQuery(id+"F0.wireOp",EDGE,"E11.11.1"),sQuery(id+"F0.wireOp",EDGE,"E11.11.2"),sQuery(id+"F0.wireOp",EDGE,"E11.11.3"),sQuery(id+"F0.wireOp",EDGE,"E11.11.4"),sQuery(id+"F0.wireOp",EDGE,"E11.11.5"),sQuery(id+"F0.wireOp",EDGE,"E11.11.6"),sQuery(id+"F0.wireOp",EDGE,"E11.11.7"),sQuery(id+"F0.wireOp",EDGE,"E11.11.8"),sQuery(id+"F0.wireOp",EDGE,"E11.11.9"),sQuery(id+"F0.wireOp",EDGE,"E11.12.0"),sQuery(id+"F0.wireOp",EDGE,"E11.12.1"),sQuery(id+"F0.wireOp",EDGE,"E11.12.2"),sQuery(id+"F0.wireOp",EDGE,"E11.12.3"),sQuery(id+"F0.wireOp",EDGE,"E11.12.4"),sQuery(id+"F0.wireOp",EDGE,"E11.12.5"),sQuery(id+"F0.wireOp",EDGE,"E11.12.6"),sQuery(id+"F0.wireOp",EDGE,"E11.12.7"),sQuery(id+"F0.wireOp",EDGE,"E11.12.8"),sQuery(id+"F0.wireOp",EDGE,"E11.12.9"),sQuery(id+"F0.wireOp",EDGE,"E11.13.0"),sQuery(id+"F0.wireOp",EDGE,"E11.13.1"),sQuery(id+"F0.wireOp",EDGE,"E11.13.2"),sQuery(id+"F0.wireOp",EDGE,"E11.13.3"),sQuery(id+"F0.wireOp",EDGE,"E11.13.4"),sQuery(id+"F0.wireOp",EDGE,"E11.13.5"),sQuery(id+"F0.wireOp",EDGE,"E11.13.6"),sQuery(id+"F0.wireOp",EDGE,"E11.13.7"),sQuery(id+"F0.wireOp",EDGE,"E11.13.8"),sQuery(id+"F0.wireOp",EDGE,"E11.13.9"),sQuery(id+"F0.wireOp",EDGE,"E11.14.0"),sQuery(id+"F0.wireOp",EDGE,"E11.14.1"),sQuery(id+"F0.wireOp",EDGE,"E11.14.2"),sQuery(id+"F0.wireOp",EDGE,"E11.14.3"),sQuery(id+"F0.wireOp",EDGE,"E11.14.4"),sQuery(id+"F0.wireOp",EDGE,"E11.14.5"),sQuery(id+"F0.wireOp",EDGE,"E11.14.6"),sQuery(id+"F0.wireOp",EDGE,"E11.14.7"),sQuery(id+"F0.wireOp",EDGE,"E11.14.8"),sQuery(id+"F0.wireOp",EDGE,"E11.14.9"),sQuery(id+"F0.wireOp",EDGE,"E11.15.0"),sQuery(id+"F0.wireOp",EDGE,"E11.15.1"),sQuery(id+"F0.wireOp",EDGE,"E11.15.2"),sQuery(id+"F0.wireOp",EDGE,"E11.15.3"),sQuery(id+"F0.wireOp",EDGE,"E11.15.4"),sQuery(id+"F0.wireOp",EDGE,"E11.15.5"),sQuery(id+"F0.wireOp",EDGE,"E11.15.6"),sQuery(id+"F0.wireOp",EDGE,"E11.15.7"),sQuery(id+"F0.wireOp",EDGE,"E11.15.8"),sQuery(id+"F0.wireOp",EDGE,"E11.15.9"),sQuery(id+"F0.wireOp",EDGE,"E11.16.0"),sQuery(id+"F0.wireOp",EDGE,"E11.16.1"),sQuery(id+"F0.wireOp",EDGE,"E11.16.2"),sQuery(id+"F0.wireOp",EDGE,"E11.16.3"),sQuery(id+"F0.wireOp",EDGE,"E11.16.4"),sQuery(id+"F0.wireOp",EDGE,"E11.16.5"),sQuery(id+"F0.wireOp",EDGE,"E11.16.6"),sQuery(id+"F0.wireOp",EDGE,"E11.16.7"),sQuery(id+"F0.wireOp",EDGE,"E11.16.8"),sQuery(id+"F0.wireOp",EDGE,"E11.16.9"),sQuery(id+"F0.wireOp",EDGE,"E11.17.0"),sQuery(id+"F0.wireOp",EDGE,"E11.17.1"),sQuery(id+"F0.wireOp",EDGE,"E11.17.2"),sQuery(id+"F0.wireOp",EDGE,"E11.17.3"),sQuery(id+"F0.wireOp",EDGE,"E11.17.4"),sQuery(id+"F0.wireOp",EDGE,"E11.17.5"),sQuery(id+"F0.wireOp",EDGE,"E11.17.6"),sQuery(id+"F0.wireOp",EDGE,"E11.17.7"),sQuery(id+"F0.wireOp",EDGE,"E11.17.8"),sQuery(id+"F0.wireOp",EDGE,"E11.17.9"),sQuery(id+"F0.wireOp",EDGE,"E11.18.0"),sQuery(id+"F0.wireOp",EDGE,"E11.18.1"),sQuery(id+"F0.wireOp",EDGE,"E11.18.2"),sQuery(id+"F0.wireOp",EDGE,"E11.18.3"),sQuery(id+"F0.wireOp",EDGE,"E11.18.4"),sQuery(id+"F0.wireOp",EDGE,"E11.18.5"),sQuery(id+"F0.wireOp",EDGE,"E11.18.6"),sQuery(id+"F0.wireOp",EDGE,"E11.18.7"),sQuery(id+"F0.wireOp",EDGE,"E11.18.8"),sQuery(id+"F0.wireOp",EDGE,"E11.18.9"),sQuery(id+"F0.wireOp",EDGE,"E11.19.0"),sQuery(id+"F0.wireOp",EDGE,"E11.19.1"),sQuery(id+"F0.wireOp",EDGE,"E11.19.2"),sQuery(id+"F0.wireOp",EDGE,"E11.19.3"),sQuery(id+"F0.wireOp",EDGE,"E11.19.4"),sQuery(id+"F0.wireOp",EDGE,"E11.19.5"),sQuery(id+"F0.wireOp",EDGE,"E11.19.6"),sQuery(id+"F0.wireOp",EDGE,"E11.19.7"),sQuery(id+"F0.wireOp",EDGE,"E11.19.8"),sQuery(id+"F0.wireOp",EDGE,"E11.19.9"),sQuery(id+"F0.wireOp",EDGE,"E12.trimOffspring"),sQuery(id+"F0.wireOp",EDGE,"E13.trimOffspring"),sQuery(id+"F0.wireOp",EDGE,"E14.trimOffspring"),sQuery(id+"F0.wireOp",EDGE,"E15.trimOffspring"),sQuery(id+"F0.wireOp",EDGE,"E16.trimOffspring")])],"isStart":false});
            var sketch = newSketch(context, id + "F2", { "sketchPlane" : qUnion([Q0])});
            skCircle(sketch, "E17", {"center": v(0, 0) * mm, "radius": 6.35 * mm});
            skSolve(sketch);
        }
        {
            var Q0;
            Q0 = qSketchRegion(id + "F2", true);
            extrude(context, id + "F3", {"entities" : qUnion([Q0]), "operationType" : NewBodyOperationType.REMOVE, "endBound" : BoundingType.THROUGH_ALL, "oppositeDirection" : true, "depth" : 25.4 * mm});
        }
    });
